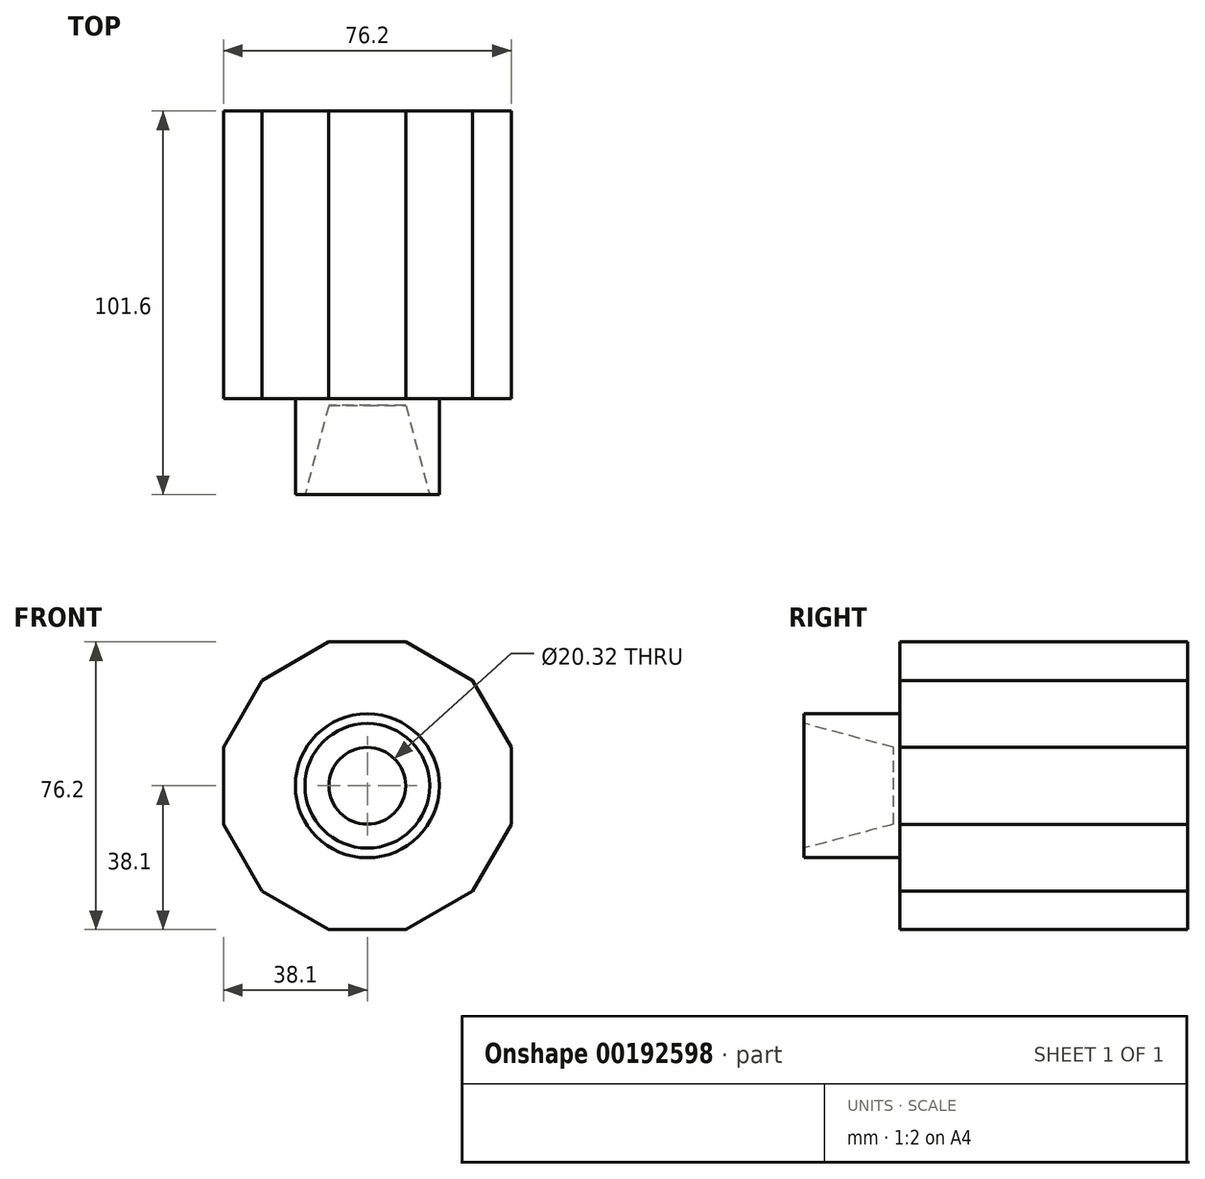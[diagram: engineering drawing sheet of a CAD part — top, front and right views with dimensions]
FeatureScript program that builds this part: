
annotation { "Feature Type Name" : "Feature", "Feature Type Description" : "" }
export const myFeature = defineFeature(function(context is Context, id is Id, definition is map)
    precondition{}
    {
        {
            var Q0;
            Q0=qCreatedBy(makeId("Front.planeOp"),FACE);
            var sketch = newSketch(context, id + "F0", { "sketchPlane" : qUnion([Q0])});
            skCircle(sketch, "E0.cCircle", {"center": v(0, 0) * mm, "radius": 38.1 * mm, "construction": true});
            skLineSegment(sketch, "E0.0", {"start": v(-38.1, -10.2) * mm, "end": v(-38.1, 10.2) * mm});
            skLineSegment(sketch, "E0.1", {"start": v(-38.1, 10.2) * mm, "end": v(-27.9, 27.9) * mm});
            skLineSegment(sketch, "E0.2", {"start": v(-27.9, 27.9) * mm, "end": v(-10.2, 38.1) * mm});
            skLineSegment(sketch, "E0.3", {"start": v(-10.2, 38.1) * mm, "end": v(10.2, 38.1) * mm});
            skLineSegment(sketch, "E0.4", {"start": v(10.2, 38.1) * mm, "end": v(27.9, 27.9) * mm});
            skLineSegment(sketch, "E0.5", {"start": v(27.9, 27.9) * mm, "end": v(38.1, 10.2) * mm});
            skLineSegment(sketch, "E0.6", {"start": v(38.1, 10.2) * mm, "end": v(38.1, -10.2) * mm});
            skLineSegment(sketch, "E0.7", {"start": v(38.1, -10.2) * mm, "end": v(27.9, -27.9) * mm});
            skLineSegment(sketch, "E0.8", {"start": v(27.9, -27.9) * mm, "end": v(10.2, -38.1) * mm});
            skLineSegment(sketch, "E0.9", {"start": v(10.2, -38.1) * mm, "end": v(-10.2, -38.1) * mm});
            skLineSegment(sketch, "E0.10", {"start": v(-10.2, -38.1) * mm, "end": v(-27.9, -27.9) * mm});
            skLineSegment(sketch, "E0.11", {"start": v(-27.9, -27.9) * mm, "end": v(-38.1, -10.2) * mm});
            skPoint(sketch, "E0.0.midPoint", {"position": v(-38.1, 0) * mm});
            skSolve(sketch);
        }
        {
            var Q0;
            Q0 = qSketchRegion(id + "F0", true);
            extrude(context, id + "F1", {"entities" : qUnion([Q0]), "oppositeDirection" : true, "depth" : 76.2 * mm});
        }
        {
            var Q0;
            Q0=qCreatedBy(makeId("Front.planeOp"),FACE);
            var sketch = newSketch(context, id + "F2", { "sketchPlane" : qUnion([Q0])});
            skCircle(sketch, "E1", {"center": v(0, 0) * mm, "radius": 19.05 * mm});
            skSolve(sketch);
        }
        {
            var Q0;
            Q0 = qSketchRegion(id + "F2", true);
            extrude(context, id + "F3", {"entities" : qUnion([Q0]), "operationType" : NewBodyOperationType.ADD, "depth" : 25.4 * mm});
        }
        {
            var Q0;
            Q0=makeQuery(id+"F3.opExtrude","CAP_FACE",FACE,{"disambiguationData":[OSD([sQuery(id+"F2.wireOp",EDGE,"E1")])],"isStart":false});
            var sketch = newSketch(context, id + "F4", { "sketchPlane" : qUnion([Q0])});
            skCircle(sketch, "E2", {"center": v(0, 0) * mm, "radius": 10.16 * mm});
            skSolve(sketch);
        }
        {
            var Q0;
            Q0 = qSketchRegion(id + "F4", true);
            extrude(context, id + "F5", {"entities" : qUnion([Q0]), "operationType" : NewBodyOperationType.REMOVE, "oppositeDirection" : true, "depth" : 101.6 * mm});
        }
        {
            var Q0;
            Q0=qCreatedBy(makeId("Right.planeOp"),FACE);
            var sketch = newSketch(context, id + "F6", { "sketchPlane" : qUnion([Q0])});
            skLineSegment(sketch, "E3.0", {"start": v(-25.4, -19.05) * mm, "end": v(-25.4, 19.05) * mm});
            skLineSegment(sketch, "E4", {"start": v(-25.4, 0) * mm, "end": v(-25.4, 16.51) * mm});
            skLineSegment(sketch, "E5", {"start": v(-25.4, 16.51) * mm, "end": v(36.22, 0) * mm});
            skLineSegment(sketch, "E6", {"start": v(36.22, 0) * mm, "end": v(-25.4, 0) * mm});
            skSolve(sketch);
        }
        {
            var Q0;
            Q0 = qSketchRegion(id + "F6", true);
            var Q1;
            Q1=sQuery(id+"F6.wireOp",EDGE,"E6");
            revolve(context, id + "F7", {"operationType" : NewBodyOperationType.REMOVE, "entities" : qUnion([Q0]), "axis" : qUnion([Q1]), "revolveType" : RevolveType.ONE_DIRECTION, "oppositeDirection" : true, "angle" : 360 * degree});
        }
    });
